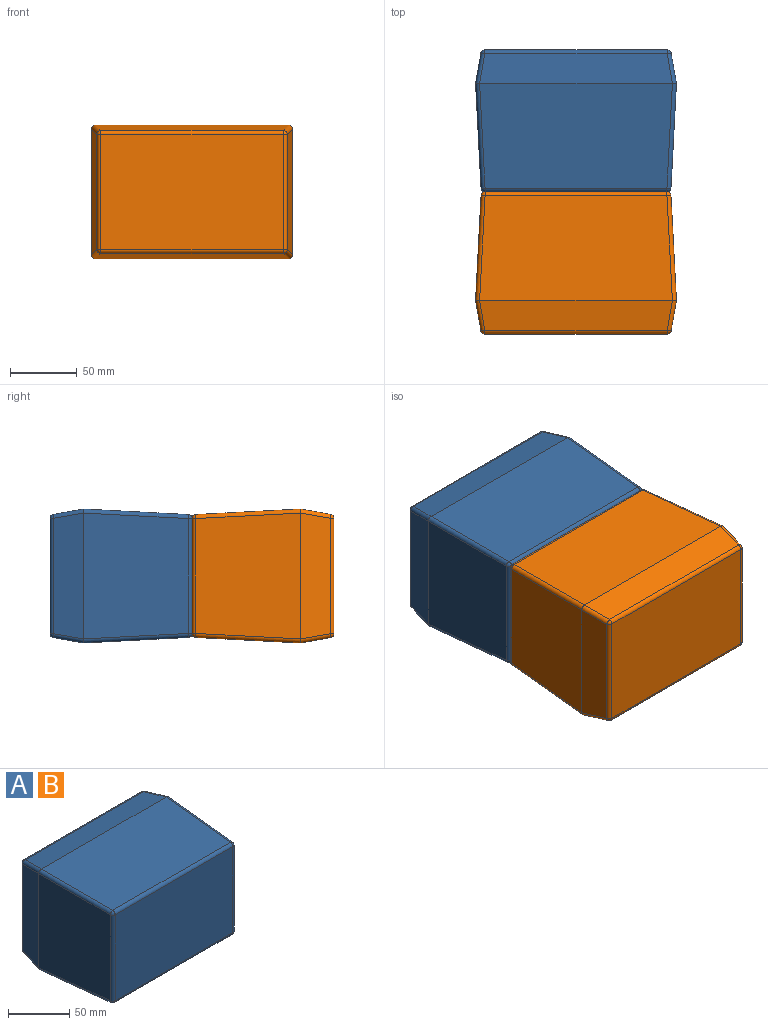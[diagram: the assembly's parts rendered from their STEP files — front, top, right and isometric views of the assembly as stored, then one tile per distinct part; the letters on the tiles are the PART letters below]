
ASSEMBLY  parts=2 mates=1
PART A: 34 faces, bbox 150x106x100 mm
  f0: plane 94.01x78.16mm, normal (-1,-0.05,0), area 7036.9mm2, adj f9,f17,f24,f31
  f1: plane 144.01x78.16mm, normal (0,-0.05,-1), area 10950.1mm2, adj f8,f15,f25,f31
  f2: plane 94.01x78.16mm, normal (1,-0.05,0), area 7036.9mm2, adj f7,f10,f14,f15
  f3: plane 144.01x78.16mm, normal (0,-0.05,1), area 10950.1mm2, adj f6,f10,f13,f17
  f4: plane 135.82x85.82mm, normal (0,-1,0), area 11655.2mm2, adj f13,f14,f24,f25
  f5: plane 136.15x86.15mm, normal (0,1,0), area 11729.1mm2, adj f21,f22,f29,f30
  f6: plane 144.09x22.52mm, normal (0,0.17,0.98), area 3204.3mm2, adj f3,f10,f12,f17,f22,f23
  f7: plane 94.09x22.52mm, normal (0.98,0.17,0), area 2060.9mm2, adj f2,f10,f12,f15,f20,f21
  f8: plane 144.09x22.52mm, normal (0,0.17,-0.98), area 3204.3mm2, adj f1,f15,f20,f29,f31,f33
  f9: plane 94.09x22.52mm, normal (-0.98,0.17,0), area 2060.9mm2, adj f0,f17,f23,f30,f31,f33
  f10: cylinder r=3mm len=78.36mm, axis (0.05,1,0.05), area 369.1mm2, adj f2,f3,f6,f7,f11,f12
  f11: sphere r=3mm, area 13.2mm2, adj f10,f13,f14
  f12: cylinder r=3mm len=22.86mm, axis (-0.17,0.97,-0.17), area 107.7mm2, adj f6,f7,f10,f16
  f13: cylinder r=3mm len=135.82mm, axis (1,0,0), area 618.7mm2, adj f3,f4,f11,f18
  f14: cylinder r=3mm len=85.82mm, axis (0,0,1), area 390.9mm2, adj f2,f4,f11,f19
  f15: cylinder r=3mm len=78.36mm, axis (0.05,1,-0.05), area 369.1mm2, adj f1,f2,f7,f8,f19,f20
  f16: sphere r=3mm, area 11mm2, adj f12,f21,f22
  f17: cylinder r=3mm len=78.36mm, axis (-0.05,1,0.05), area 369.1mm2, adj f0,f3,f6,f9,f18,f23
  f18: sphere r=3mm, area 13.2mm2, adj f13,f17,f24
  f19: sphere r=3mm, area 13.2mm2, adj f14,f15,f25
  f20: cylinder r=3mm len=22.86mm, axis (-0.17,0.97,0.17), area 107.7mm2, adj f7,f8,f15,f26
  f21: cylinder r=3mm len=86.15mm, axis (0,0,-1), area 360.9mm2, adj f5,f7,f16,f26
  f22: cylinder r=3mm len=136.15mm, axis (-1,0,0), area 570.3mm2, adj f5,f6,f16,f27
  f23: cylinder r=3mm len=22.86mm, axis (0.17,0.97,-0.17), area 107.7mm2, adj f6,f9,f17,f27
  f24: cylinder r=3mm len=85.82mm, axis (0,0,1), area 390.9mm2, adj f0,f4,f18,f28
  f25: cylinder r=3mm len=135.82mm, axis (1,0,0), area 618.7mm2, adj f1,f4,f19,f28
  f26: sphere r=3mm, area 11mm2, adj f20,f21,f29
  f27: sphere r=3mm, area 11mm2, adj f22,f23,f30
  f28: sphere r=3mm, area 13.2mm2, adj f24,f25,f31
  f29: cylinder r=3mm len=136.15mm, axis (-1,0,0), area 570.3mm2, adj f5,f8,f26,f32
  f30: cylinder r=3mm len=86.15mm, axis (0,0,-1), area 360.9mm2, adj f5,f9,f27,f32
  f31: cylinder r=3mm len=78.36mm, axis (-0.05,1,-0.05), area 369.1mm2, adj f0,f1,f8,f9,f28,f33
  f32: sphere r=3mm, area 11mm2, adj f29,f30,f33
  f33: cylinder r=3mm len=22.86mm, axis (0.17,0.97,0.17), area 107.7mm2, adj f8,f9,f31,f32
PART B: same geometry as A
PLACE A t=(-26.38,87.16,-24.81)mm fixed
PLACE B rot(axis=(1,0,0),180deg) t=(-26.38,-74.84,75.19)mm
MATE planar B.f4 <-> A.f4  axis (0,1,0) through (48.62,6.16,25.19)mm
